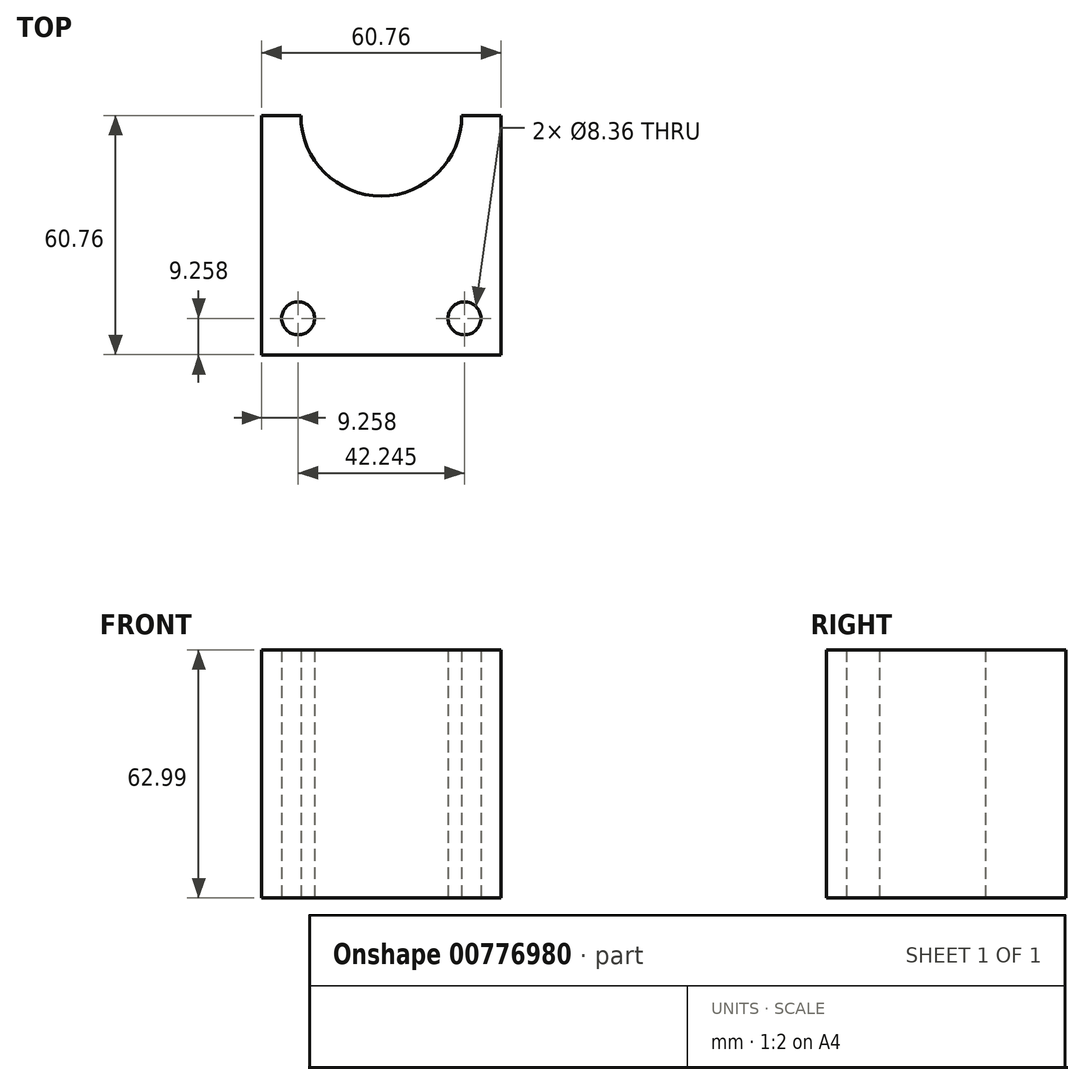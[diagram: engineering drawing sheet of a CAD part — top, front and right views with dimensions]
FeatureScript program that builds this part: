
annotation { "Feature Type Name" : "Feature", "Feature Type Description" : "" }
export const myFeature = defineFeature(function(context is Context, id is Id, definition is map)
    precondition{}
    {
        {
            var Q0;
            Q0=qCreatedBy(makeId("Top.planeOp"),FACE);
            var sketch = newSketch(context, id + "F0", { "sketchPlane" : qUnion([Q0])});
            skLineSegment(sketch, "E0.bottom", {"start": v(30.38, -30.38) * mm, "end": v(-30.38, -30.38) * mm});
            skLineSegment(sketch, "E0.top", {"start": v(30.38, 30.38) * mm, "end": v(20.44, 30.38) * mm});
            skLineSegment(sketch, "E0.left", {"start": v(30.38, -30.38) * mm, "end": v(30.38, 30.38) * mm});
            skLineSegment(sketch, "E0.right", {"start": v(-30.38, -30.38) * mm, "end": v(-30.38, 30.38) * mm});
            skPoint(sketch, "E0.middle", {"position": v(0, 0) * mm});
            skArc(sketch, "E1", {"start": v(-20.44, 30.38) * mm, "mid": v(0, 9.95) * mm, "end": v(20.44, 30.38) * mm});
            skLineSegment(sketch, "E2.trimOffspring", {"start": v(-20.44, 30.38) * mm, "end": v(-30.38, 30.38) * mm});
            skCircle(sketch, "E3", {"center": v(21.12, -21.12) * mm, "radius": 4.18 * mm});
            skCircle(sketch, "E4.MirrorC", {"center": v(-21.12, -21.12) * mm, "radius": 4.18 * mm});
            skSolve(sketch);
        }
        {
            var Q0;
            Q0=makeQuery(id+"F0.imprint","IMPRINT",FACE,{"disambiguationData":[TD([[makeQuery(id+"F0.imprint","IMPRINT",EDGE,{"derivedFrom":sQuery(id+"F0.wireOp",EDGE,"E0.bottom")}),-1.0]])]});
            extrude(context, id + "F1", {"entities" : qUnion([Q0]), "depth" : 63 * mm, "offsetDistance" : 25.4 * mm});
        }
    });
